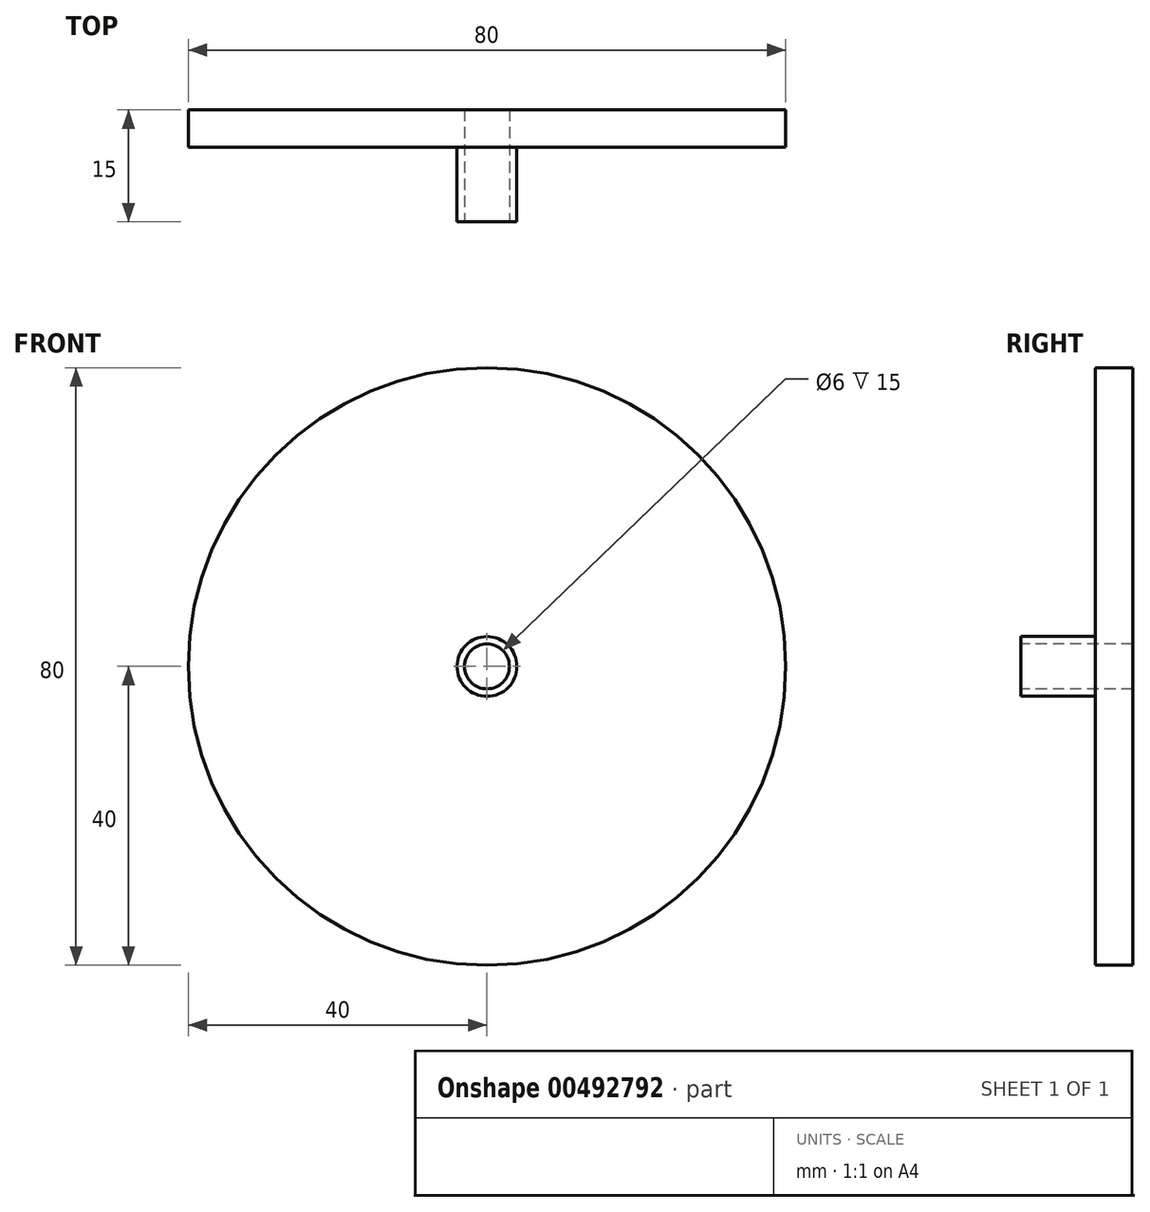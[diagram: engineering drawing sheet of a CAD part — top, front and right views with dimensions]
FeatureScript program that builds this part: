
annotation { "Feature Type Name" : "Feature", "Feature Type Description" : "" }
export const myFeature = defineFeature(function(context is Context, id is Id, definition is map)
    precondition{}
    {
        {
            var Q0;
            Q0=qCreatedBy(makeId("Front.planeOp"),FACE);
            var sketch = newSketch(context, id + "F0", { "sketchPlane" : qUnion([Q0])});
            skCircle(sketch, "E0", {"center": v(0, 0) * mm, "radius": 40 * mm});
            skSolve(sketch);
        }
        {
            var Q0;
            Q0 = qSketchRegion(id + "F0", true);
            extrude(context, id + "F1", {"entities" : qUnion([Q0]), "depth" : 5 * mm, "offsetDistance" : 25 * mm});
        }
        {
            var Q0;
            Q0=makeQuery(id+"F1.opExtrude","CAP_FACE",FACE,{"disambiguationData":[OSD([sQuery(id+"F0.wireOp",EDGE,"E0")])],"isStart":false});
            var sketch = newSketch(context, id + "F2", { "sketchPlane" : qUnion([Q0])});
            skCircle(sketch, "E1", {"center": v(0, 0) * mm, "radius": 4 * mm});
            skSolve(sketch);
        }
        {
            var Q0;
            Q0 = qSketchRegion(id + "F2", true);
            extrude(context, id + "F3", {"entities" : qUnion([Q0]), "operationType" : NewBodyOperationType.ADD, "depth" : 10 * mm, "offsetDistance" : 25 * mm});
        }
        {
            var Q0;
            Q0=makeQuery(id+"F3.opExtrude","CAP_FACE",FACE,{"disambiguationData":[OSD([sQuery(id+"F2.wireOp",EDGE,"E1")])],"isStart":false});
            var sketch = newSketch(context, id + "F4", { "sketchPlane" : qUnion([Q0])});
            skCircle(sketch, "E2", {"center": v(0, 0) * mm, "radius": 3 * mm});
            skSolve(sketch);
        }
        {
            var Q0;
            Q0 = qSketchRegion(id + "F4", true);
            extrude(context, id + "F5", {"entities" : qUnion([Q0]), "operationType" : NewBodyOperationType.REMOVE, "oppositeDirection" : true, "depth" : 25 * mm, "offsetDistance" : 25 * mm});
        }
    });
